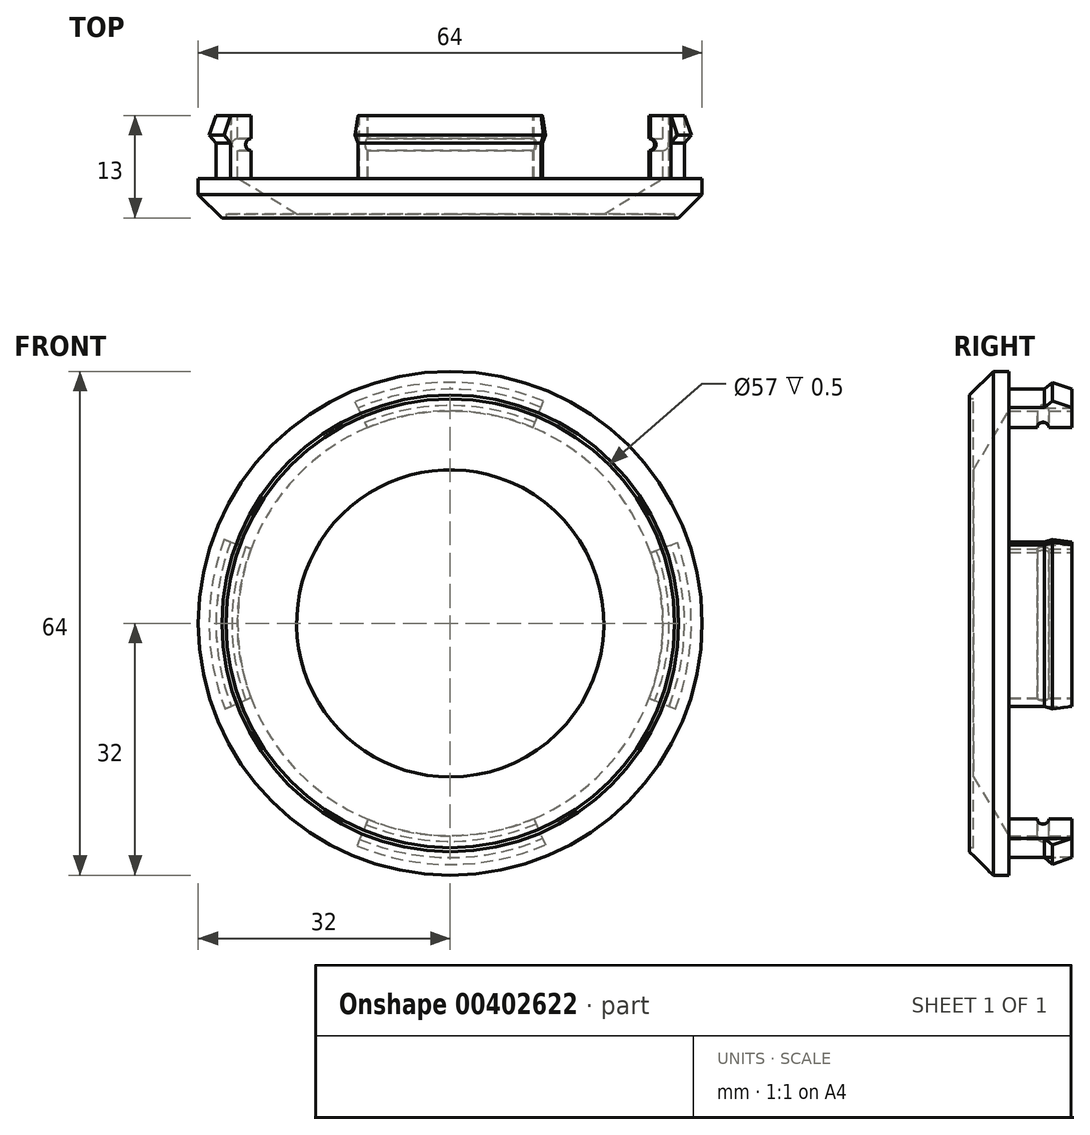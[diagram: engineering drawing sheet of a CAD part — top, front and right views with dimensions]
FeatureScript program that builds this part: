
annotation { "Feature Type Name" : "Feature", "Feature Type Description" : "" }
export const myFeature = defineFeature(function(context is Context, id is Id, definition is map)
    precondition{}
    {
        {
            var Q0;
            Q0=qCreatedBy(makeId("Front.planeOp"),FACE);
            var sketch = newSketch(context, id + "F0", { "sketchPlane" : qUnion([Q0])});
            skCircle(sketch, "E0", {"center": v(0, 0) * mm, "radius": 32 * mm});
            skSolve(sketch);
        }
        {
            var Q0;
            Q0=makeQuery(id+"F0.imprint","IMPRINT",FACE,{"disambiguationData":[TD([[makeQuery(id+"F0.imprint","IMPRINT",EDGE,{"derivedFrom":sQuery(id+"F0.wireOp",EDGE,"E0")}),1.0]])]});
            extrude(context, id + "F1", {"entities" : qUnion([Q0]), "depth" : 5 * mm});
        }
        {
            var Q0;
            Q0=makeQuery(id+"F1.opExtrude","CAP_EDGE",EDGE,{"disambiguationData":[OSD([sQuery(id+"F0.wireOp",EDGE,"E0")])],"isStart":false});
            chamfer(context, id + "F2", {"entities" : qUnion([Q0]), "width" : 3 * mm, "tangentPropagation" : true});
        }
        {
            var Q0;
            Q0=makeQuery(id+"F1.opExtrude","CAP_FACE",FACE,{"disambiguationData":[OSD([sQuery(id+"F0.wireOp",EDGE,"E0")])],"isStart":true});
            var sketch = newSketch(context, id + "F3", { "sketchPlane" : qUnion([Q0])});
            skCircle(sketch, "E1", {"center": v(0, 0) * mm, "radius": 29.75 * mm});
            skSolve(sketch);
        }
        {
            var Q0;
            Q0=makeQuery(id+"F3.imprint","IMPRINT",FACE,{"disambiguationData":[TD([[makeQuery(id+"F3.imprint","IMPRINT",EDGE,{"derivedFrom":sQuery(id+"F3.wireOp",EDGE,"E1")}),1.0]])]});
            extrude(context, id + "F4", {"entities" : qUnion([Q0]), "operationType" : NewBodyOperationType.ADD, "depth" : 8 * mm});
        }
        {
            var Q0;
            Q0=makeQuery(id+"F4.opExtrude","CAP_FACE",FACE,{"disambiguationData":[OSD([sQuery(id+"F3.wireOp",EDGE,"E1")])],"isStart":false});
            var sketch = newSketch(context, id + "F5", { "sketchPlane" : qUnion([Q0])});
            skCircle(sketch, "E2", {"center": v(0, 0) * mm, "radius": 27 * mm});
            skSolve(sketch);
        }
        {
            var Q0;
            Q0=sQuery(id+"F5.wireOp",VERTEX,"E2.center");
            var Q1;
            Q1=makeQuery(id+"F1.opExtrude","SWEPT_BODY",BODY,{"disambiguationData":[OSD([sQuery(id+"F0.wireOp",EDGE,"E0")])]});
            hole(context, id + "F6", {"style" : HoleStyle.SIMPLE, "endStyle" : HoleEndStyle.BLIND, "holeDiameter" : 54 * mm, "holeDepth" : 8 * mm, "isTappedThrough" : true, "tappedDepth" : 12 * mm, "tapClearance" : 3, "locations" : qUnion([Q0]), "scope" : qUnion([Q1])});
        }
        {
            var Q0;
            Q0=makeQuery(id+"F4.opExtrude","CAP_FACE",FACE,{"disambiguationData":[OSD([sQuery(id+"F3.wireOp",EDGE,"E1")])],"isStart":false});
            var sketch = newSketch(context, id + "F7", { "sketchPlane" : qUnion([Q0])});
            skSolve(sketch);
        }
        {
            var Q0;
            Q0=makeQuery(id+"F7.imprint","IMPRINT",FACE,{"disambiguationData":[TD([[makeQuery(id+"F7.imprint","IMPRINT",EDGE,{"derivedFrom":makeQuery(id+"F4.opExtrude","CAP_EDGE",EDGE,{"disambiguationData":[OSD([sQuery(id+"F3.wireOp",EDGE,"E1")])],"isStart":false})}),1.0]])]});
            var sketch = newSketch(context, id + "F8", { "sketchPlane" : qUnion([Q0])});
            skLineSegment(sketch, "E3", {"start": v(-24.39, 8.56) * mm, "end": v(-30.58, 10.98) * mm});
            skLineSegment(sketch, "E4", {"start": v(-9.97, 23.51) * mm, "end": v(-12.66, 30.25) * mm});
            skLineSegment(sketch, "E5", {"start": v(12.66, 29.44) * mm, "end": v(9.7, 23.1) * mm});
            skLineSegment(sketch, "E6", {"start": v(30.45, 11.25) * mm, "end": v(23.44, 8.82) * mm});
            skLineSegment(sketch, "E7", {"start": v(-24.25, -9.1) * mm, "end": v(-29.91, -11.38) * mm});
            skLineSegment(sketch, "E8", {"start": v(-9.97, -23.38) * mm, "end": v(-12.8, -29.7) * mm});
            skLineSegment(sketch, "E9", {"start": v(9.84, -23.38) * mm, "end": v(12.66, -30.25) * mm});
            skLineSegment(sketch, "E10", {"start": v(23.3, -8.56) * mm, "end": v(30.18, -11.65) * mm});
            skLineSegment(sketch, "E11", {"start": v(-12.66, 30.25) * mm, "end": v(-24.6, 22.51) * mm});
            skLineSegment(sketch, "E12", {"start": v(-24.6, 22.51) * mm, "end": v(-30.58, 10.98) * mm});
            skLineSegment(sketch, "E13", {"start": v(-24.39, 8.56) * mm, "end": v(-9.97, 23.51) * mm});
            skSolve(sketch);
        }
        {
            var Q0;
            Q0=makeQuery(id+"F1.opExtrude","CAP_FACE",FACE,{"disambiguationData":[OSD([sQuery(id+"F0.wireOp",EDGE,"E0")])],"isStart":false});
            var sketch = newSketch(context, id + "F9", { "sketchPlane" : qUnion([Q0])});
            skCircle(sketch, "E14", {"center": v(0, 0) * mm, "radius": 28.5 * mm});
            skSolve(sketch);
        }
        {
            var Q0;
            Q0 = qSketchRegion(id + "F9", true);
            extrude(context, id + "F10", {"entities" : qUnion([Q0]), "operationType" : NewBodyOperationType.REMOVE, "oppositeDirection" : true, "depth" : 0.5 * mm});
        }
        {
            var Q0;
            Q0=qCreatedBy(makeId("Top.planeOp"),FACE);
            var sketch = newSketch(context, id + "F11", { "sketchPlane" : qUnion([Q0])});
            skLineSegment(sketch, "E15", {"start": v(0, 10.98) * mm, "end": v(0, -11.92) * mm});
            skSolve(sketch);
        }
        {
            var Q0;
            {var subQ0=sQuery(id+"F8.wireOp",EDGE,"E3");var subQ1=makeQuery(id+"F7.imprint","IMPRINT",EDGE,{"derivedFrom":makeQuery(id+"F4.opExtrude","CAP_EDGE",EDGE,{"disambiguationData":[OSD([sQuery(id+"F3.wireOp",EDGE,"E1")])],"isStart":false})});var subQ2=makeQuery(id+"F8.imprint","INTERSECT",VERTEX,{"derivedFrom":[subQ1,subQ0]});Q0=makeQuery(id+"F8.imprint","IMPRINT",FACE,{"disambiguationData":[TD([[makeQuery(id+"F8.imprint","IMPRINT",EDGE,{"disambiguationData":[TD([[subQ2,1.0]])],"derivedFrom":subQ1}),1.0]])]});}
            var Q1;
            {var subQ0=sQuery(id+"F8.wireOp",EDGE,"E5");var subQ1=makeQuery(id+"F7.imprint","IMPRINT",EDGE,{"derivedFrom":makeQuery(id+"F4.opExtrude","CAP_EDGE",EDGE,{"disambiguationData":[OSD([sQuery(id+"F3.wireOp",EDGE,"E1")])],"isStart":false})});var subQ2=makeQuery(id+"F8.imprint","INTERSECT",VERTEX,{"derivedFrom":[subQ1,subQ0]});Q1=makeQuery(id+"F8.imprint","IMPRINT",FACE,{"disambiguationData":[TD([[makeQuery(id+"F8.imprint","IMPRINT",EDGE,{"disambiguationData":[TD([[subQ2,1.0]])],"derivedFrom":subQ1}),1.0]])]});}
            var Q2;
            {var subQ0=sQuery(id+"F8.wireOp",EDGE,"E9");var subQ1=makeQuery(id+"F7.imprint","IMPRINT",EDGE,{"derivedFrom":makeQuery(id+"F4.opExtrude","CAP_EDGE",EDGE,{"disambiguationData":[OSD([sQuery(id+"F3.wireOp",EDGE,"E1")])],"isStart":false})});var subQ2=makeQuery(id+"F8.imprint","INTERSECT",VERTEX,{"derivedFrom":[subQ1,subQ0]});Q2=makeQuery(id+"F8.imprint","IMPRINT",FACE,{"disambiguationData":[TD([[makeQuery(id+"F8.imprint","IMPRINT",EDGE,{"disambiguationData":[TD([[subQ2,-1.0]])],"derivedFrom":subQ1}),1.0]])]});}
            var Q3;
            {var subQ0=sQuery(id+"F8.wireOp",EDGE,"E7");var subQ1=makeQuery(id+"F7.imprint","IMPRINT",EDGE,{"derivedFrom":makeQuery(id+"F4.opExtrude","CAP_EDGE",EDGE,{"disambiguationData":[OSD([sQuery(id+"F3.wireOp",EDGE,"E1")])],"isStart":false})});var subQ2=makeQuery(id+"F8.imprint","INTERSECT",VERTEX,{"derivedFrom":[subQ1,subQ0]});Q3=makeQuery(id+"F8.imprint","IMPRINT",FACE,{"disambiguationData":[TD([[makeQuery(id+"F8.imprint","IMPRINT",EDGE,{"disambiguationData":[TD([[subQ2,-1.0]])],"derivedFrom":subQ1}),1.0]])]});}
            extrude(context, id + "F12", {"entities" : qUnion([Q0, Q1, Q2, Q3]), "operationType" : NewBodyOperationType.REMOVE, "oppositeDirection" : true, "depth" : 8 * mm});
        }
        {
            var Q0;
            Q0=makeQuery(id+"F12.boolean.opBoolean","COPY",FACE,{"derivedFrom":makeQuery(id+"F12.opExtrude","SWEPT_FACE",FACE,{"disambiguationData":[OSD([sQuery(id+"F8.wireOp",EDGE,"E4")])]})});
            var sketch = newSketch(context, id + "F13", { "sketchPlane" : qUnion([Q0])});
            skLineSegment(sketch, "E16", {"start": v(8, 29.75) * mm, "end": v(5.52, 30.62) * mm});
            skLineSegment(sketch, "E17", {"start": v(5.52, 30.62) * mm, "end": v(4.49, 29.75) * mm});
            skLineSegment(sketch, "E18", {"start": v(4.49, 29.75) * mm, "end": v(8, 29.75) * mm});
            skSolve(sketch);
        }
        {
            var Q0;
            Q0=makeQuery(id+"F13.imprint","IMPRINT",FACE,{"disambiguationData":[TD([[makeQuery(id+"F13.imprint","IMPRINT",EDGE,{"derivedFrom":sQuery(id+"F13.wireOp",EDGE,"E16")}),1.0]])]});
            var Q1;
            Q1=sQuery(id+"F11.wireOp",EDGE,"E15");
            revolve(context, id + "F14", {"operationType" : NewBodyOperationType.ADD, "entities" : qUnion([Q0]), "axis" : qUnion([Q1]), "revolveType" : RevolveType.ONE_DIRECTION, "angle" : 46 * degree});
        }
        {
            var Q0;
            Q0=makeQuery(id+"F12.boolean.opBoolean","COPY",FACE,{"derivedFrom":makeQuery(id+"F12.opExtrude","SWEPT_FACE",FACE,{"disambiguationData":[OSD([sQuery(id+"F8.wireOp",EDGE,"E7")])]})});
            var sketch = newSketch(context, id + "F15", { "sketchPlane" : qUnion([Q0])});
            skLineSegment(sketch, "E19", {"start": v(29.74, -8) * mm, "end": v(30.62, -5.52) * mm});
            skLineSegment(sketch, "E20", {"start": v(30.62, -5.52) * mm, "end": v(29.74, -4.49) * mm});
            skLineSegment(sketch, "E21", {"start": v(29.74, -4.49) * mm, "end": v(29.74, -8) * mm});
            skSolve(sketch);
        }
        {
            var Q0;
            {var subQ0=sQuery(id+"F15.wireOp",EDGE,"E20");var subQ1=sQuery(id+"F15.wireOp",EDGE,"E19");var subQ2=makeQuery(id+"F15.imprint","INTERSECT",VERTEX,{"derivedFrom":[subQ1,subQ0]});Q0=makeQuery(id+"F15.imprint","IMPRINT",FACE,{"disambiguationData":[TD([[makeQuery(id+"F15.imprint","IMPRINT",EDGE,{"disambiguationData":[TD([[subQ2,1.0]])],"derivedFrom":subQ1}),1.0]])]});}
            var Q1;
            Q1=sQuery(id+"F11.wireOp",EDGE,"E15");
            revolve(context, id + "F16", {"entities" : qUnion([Q0]), "axis" : qUnion([Q1]), "revolveType" : RevolveType.ONE_DIRECTION, "angle" : 40.35 * degree});
        }
        {
            var Q0;
            Q0=makeQuery(id+"F14.boolean.opBoolean","MERGE",FACE,{"derivedFrom":[makeQuery(id+"F12.boolean.opBoolean","COPY",FACE,{"derivedFrom":makeQuery(id+"F12.opExtrude","SWEPT_FACE",FACE,{"disambiguationData":[OSD([sQuery(id+"F8.wireOp",EDGE,"E4")])]})}),makeQuery(id+"F14.opRevolve","CAP_FACE",FACE,{"disambiguationData":[OSD([sQuery(id+"F13.wireOp",EDGE,"E16"),sQuery(id+"F13.wireOp",EDGE,"E17"),sQuery(id+"F13.wireOp",EDGE,"E18")])],"isStart":true})]});
            var sketch = newSketch(context, id + "F17", { "sketchPlane" : qUnion([Q0])});
            skCircle(sketch, "E22", {"center": v(4.32, 27) * mm, "radius": 0.74 * mm});
            skSolve(sketch);
        }
        {
            var Q0;
            {var subQ0=sQuery(id+"F17.wireOp",EDGE,"E22");var subQ1=makeQuery(id+"F12.boolean.opBoolean","COPY",EDGE,{"derivedFrom":makeQuery(id+"F12.opExtrude","SWEPT_EDGE",EDGE,{"disambiguationData":[OSD([sQuery(id+"F6.hole-0.sketch.wireOp",EDGE,"core_line_2"),sQuery(id+"F6.hole-0.sketch.wireOp",EDGE,"core_line_3"),sQuery(id+"F8.wireOp",EDGE,"E4")])]})});var subQ2=makeQuery(id+"F17.imprint","INTERSECT",VERTEX,{"disambiguationData":[OD(0.0)],"derivedFrom":[subQ1,subQ0]});Q0=makeQuery(id+"F17.imprint","IMPRINT",FACE,{"disambiguationData":[TD([[makeQuery(id+"F17.imprint","IMPRINT",EDGE,{"disambiguationData":[TD([[subQ2,1.0]])],"derivedFrom":subQ0}),1.0]])]});}
            var Q1;
            {var subQ0=sQuery(id+"F17.wireOp",EDGE,"E22");var subQ1=makeQuery(id+"F12.boolean.opBoolean","COPY",EDGE,{"derivedFrom":makeQuery(id+"F12.opExtrude","SWEPT_EDGE",EDGE,{"disambiguationData":[OSD([sQuery(id+"F6.hole-0.sketch.wireOp",EDGE,"core_line_2"),sQuery(id+"F6.hole-0.sketch.wireOp",EDGE,"core_line_3"),sQuery(id+"F8.wireOp",EDGE,"E4")])]})});var subQ2=makeQuery(id+"F17.imprint","INTERSECT",VERTEX,{"disambiguationData":[OD(0.0)],"derivedFrom":[subQ1,subQ0]});Q1=makeQuery(id+"F17.imprint","IMPRINT",FACE,{"disambiguationData":[TD([[makeQuery(id+"F17.imprint","IMPRINT",EDGE,{"disambiguationData":[TD([[subQ2,-1.0]])],"derivedFrom":subQ0}),1.0]])]});}
            var Q2;
            Q2=sQuery(id+"F11.wireOp",EDGE,"E15");
            revolve(context, id + "F18", {"operationType" : NewBodyOperationType.REMOVE, "entities" : qUnion([Q0, Q1]), "axis" : qUnion([Q2]), "revolveType" : RevolveType.FULL, "oppositeDirection" : true});
        }
        {
            var Q0;
            Q0=makeQuery(id+"F12.boolean.opBoolean","COPY",FACE,{"derivedFrom":makeQuery(id+"F12.opExtrude","SWEPT_FACE",FACE,{"disambiguationData":[OSD([sQuery(id+"F8.wireOp",EDGE,"E6")])]})});
            var sketch = newSketch(context, id + "F19", { "sketchPlane" : qUnion([Q0])});
            skLineSegment(sketch, "E23", {"start": v(-29.74, 8) * mm, "end": v(-30.61, 5.52) * mm});
            skLineSegment(sketch, "E24", {"start": v(-30.61, 5.52) * mm, "end": v(-29.74, 4.49) * mm});
            skLineSegment(sketch, "E25", {"start": v(-29.74, 4.49) * mm, "end": v(-29.74, 8) * mm});
            skSolve(sketch);
        }
        {
            var Q0;
            {var subQ0=sQuery(id+"F19.wireOp",EDGE,"E24");var subQ1=sQuery(id+"F19.wireOp",EDGE,"E23");var subQ2=makeQuery(id+"F19.imprint","INTERSECT",VERTEX,{"derivedFrom":[subQ1,subQ0]});Q0=makeQuery(id+"F19.imprint","IMPRINT",FACE,{"disambiguationData":[TD([[makeQuery(id+"F19.imprint","IMPRINT",EDGE,{"disambiguationData":[TD([[subQ2,1.0]])],"derivedFrom":subQ1}),1.0]])]});}
            var Q1;
            Q1=sQuery(id+"F11.wireOp",EDGE,"E15");
            revolve(context, id + "F20", {"operationType" : NewBodyOperationType.ADD, "entities" : qUnion([Q0]), "axis" : qUnion([Q1]), "revolveType" : RevolveType.ONE_DIRECTION, "angle" : 41.2 * degree});
        }
        {
            var Q0;
            Q0=makeQuery(id+"F12.boolean.opBoolean","COPY",FACE,{"derivedFrom":makeQuery(id+"F12.opExtrude","SWEPT_FACE",FACE,{"disambiguationData":[OSD([sQuery(id+"F8.wireOp",EDGE,"E9")])]})});
            var sketch = newSketch(context, id + "F21", { "sketchPlane" : qUnion([Q0])});
            skLineSegment(sketch, "E26", {"start": v(-8, -29.75) * mm, "end": v(-5.52, -30.62) * mm});
            skLineSegment(sketch, "E27", {"start": v(-5.52, -30.62) * mm, "end": v(-4.49, -29.75) * mm});
            skLineSegment(sketch, "E28", {"start": v(-4.49, -29.75) * mm, "end": v(-8, -29.75) * mm});
            skSolve(sketch);
        }
        {
            var Q0;
            Q0=makeQuery(id+"F21.imprint","IMPRINT",FACE,{"disambiguationData":[TD([[makeQuery(id+"F21.imprint","IMPRINT",EDGE,{"derivedFrom":sQuery(id+"F21.wireOp",EDGE,"E26")}),1.0]])]});
            var Q1;
            Q1=sQuery(id+"F21.wireOp",EDGE,"E26");
            var Q2;
            Q2=sQuery(id+"F21.wireOp",EDGE,"E28");
            var Q3;
            Q3=sQuery(id+"F21.wireOp",EDGE,"E27");
            var Q4;
            Q4=sQuery(id+"F11.wireOp",EDGE,"E15");
            revolve(context, id + "F22", {"entities" : qUnion([Q0]), "surfaceEntities" : qUnion([Q1, Q2, Q3]), "axis" : qUnion([Q4]), "revolveType" : RevolveType.ONE_DIRECTION, "angle" : 46 * degree});
        }
    });
